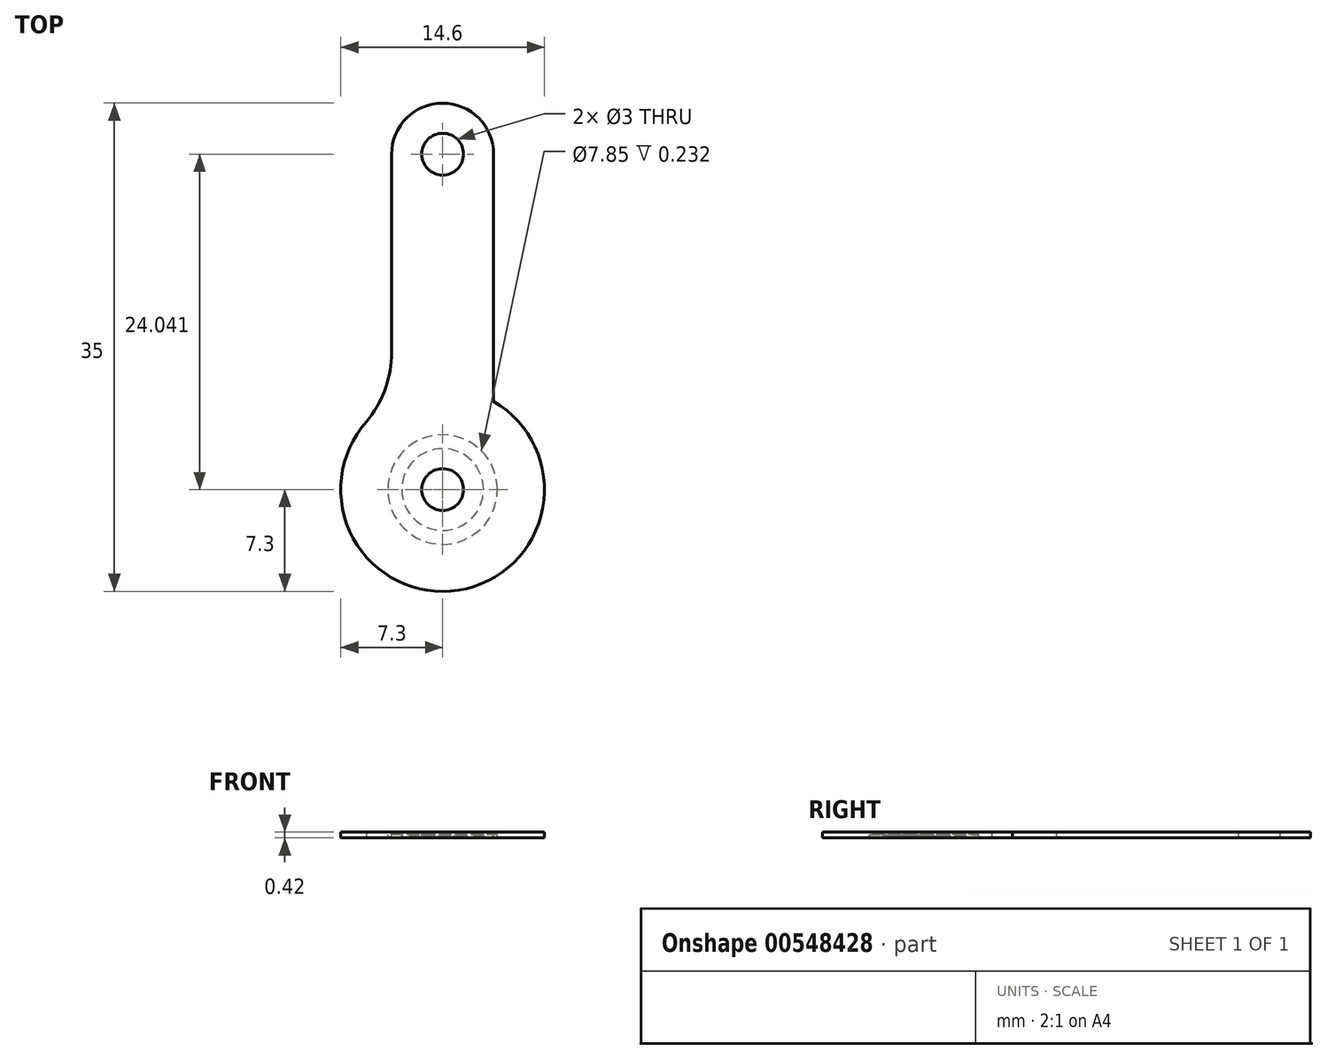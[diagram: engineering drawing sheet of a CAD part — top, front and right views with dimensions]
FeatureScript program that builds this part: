
annotation { "Feature Type Name" : "Feature", "Feature Type Description" : "" }
export const myFeature = defineFeature(function(context is Context, id is Id, definition is map)
    precondition{}
    {
        {
            assignVariable(context, id + "F0", {"name" : "HornCounterBoreDepth", "anyValue" : .42});
        }
        {
            assignVariable(context, id + "F1", {"name" : "HornThick", "anyValue" : 0.23});
        }
        {
            assignVariable(context, id + "F2", {"name" : "HornAxleHoleDepth", "anyValue" : 0.12});
        }
        {
            var Q0;
            Q0=qCreatedBy(makeId("Top.planeOp"),FACE);
            var sketch = newSketch(context, id + "F3", { "sketchPlane" : qUnion([Q0])});
            skCircle(sketch, "E0", {"center": v(0, 0) * mm, "radius": 7.3 * mm});
            skCircle(sketch, "E1", {"center": v(0, 24.04) * mm, "radius": 3.66 * mm});
            skCircle(sketch, "E2", {"center": v(0, 24.04) * mm, "radius": 1.5 * mm});
            skCircle(sketch, "E3", {"center": v(0, 0) * mm, "radius": 1.5 * mm});
            skLineSegment(sketch, "E4", {"start": v(-3.66, 24.04) * mm, "end": v(-3.66, 6.32) * mm});
            skLineSegment(sketch, "E5", {"start": v(3.66, 24.04) * mm, "end": v(3.66, 6.32) * mm});
            skArc(sketch, "E6", {"start": v(-5.43, 4.88) * mm, "mid": v(-4.18, 7.05) * mm, "end": v(-3.66, 9.5) * mm});
            skArc(sketch, "E7.MirrorCS", {"start": v(5.43, 4.88) * mm, "mid": v(4.18, 7.05) * mm, "end": v(3.66, 9.5) * mm});
            skCircle(sketch, "E8", {"center": v(0, 0) * mm, "radius": 2.93 * mm});
            skCircle(sketch, "E9", {"center": v(0, 0) * mm, "radius": 3.92 * mm});
            skSolve(sketch);
        }
        {
            var Q0;
            Q0=makeQuery(id+"F3.imprint","IMPRINT",FACE,{"disambiguationData":[TD([[makeQuery(id+"F3.imprint","IMPRINT",EDGE,{"derivedFrom":sQuery(id+"F3.wireOp",EDGE,"E2")}),-1.0]])]});
            var Q1;
            {var subQ0=sQuery(id+"F3.wireOp",EDGE,"E4");var subQ1=sQuery(id+"F3.wireOp",EDGE,"E0");var subQ2=makeQuery(id+"F3.imprint","INTERSECT",VERTEX,{"derivedFrom":[subQ1,subQ0]});Q1=makeQuery(id+"F3.imprint","IMPRINT",FACE,{"disambiguationData":[TD([[makeQuery(id+"F3.imprint","IMPRINT",EDGE,{"disambiguationData":[TD([[subQ2,1.0]])],"derivedFrom":subQ1}),-1.0]])]});}
            var Q2;
            {var subQ3=sQuery(id+"F3.wireOp",EDGE,"E6");Q2=makeQuery(id+"F3.imprint","IMPRINT",FACE,{"disambiguationData":[TD([[makeQuery(id+"F3.imprint","IMPRINT",EDGE,{"derivedFrom":subQ3}),-1.0]])]});}
            var Q3;
            {var subQ3=sQuery(id+"F3.wireOp",EDGE,"E7.MirrorCS");Q3=makeQuery(id+"F3.imprint","IMPRINT",FACE,{"disambiguationData":[TD([[makeQuery(id+"F3.imprint","IMPRINT",EDGE,{"derivedFrom":subQ3}),1.0]])]});}
            var Q4;
            Q4=makeQuery(id+"F3.imprint","IMPRINT",FACE,{"disambiguationData":[TD([[makeQuery(id+"F3.imprint","IMPRINT",EDGE,{"derivedFrom":sQuery(id+"F3.wireOp",EDGE,"E9")}),-1.0]])]});
            var Q5;
            Q5=makeQuery(id+"F3.imprint","IMPRINT",FACE,{"disambiguationData":[TD([[makeQuery(id+"F3.imprint","IMPRINT",EDGE,{"derivedFrom":sQuery(id+"F3.wireOp",EDGE,"E8")}),-1.0]])]});
            extrude(context, id + "F4", {"entities" : qUnion([Q0, Q1, Q2, Q3, Q4, Q5]), "depth" : (getVariable(context, 'HornThick') - getVariable(context, 'HornCounterBoreDepth')) * mm, "offsetDistance" : 25.4 * mm});
        }
        {
            var Q0;
            Q0=makeQuery(id+"F3.imprint","IMPRINT",FACE,{"disambiguationData":[TD([[makeQuery(id+"F3.imprint","IMPRINT",EDGE,{"derivedFrom":sQuery(id+"F3.wireOp",EDGE,"E2")}),-1.0]])]});
            var Q1;
            {var subQ3=sQuery(id+"F3.wireOp",EDGE,"E7.MirrorCS");Q1=makeQuery(id+"F3.imprint","IMPRINT",FACE,{"disambiguationData":[TD([[makeQuery(id+"F3.imprint","IMPRINT",EDGE,{"derivedFrom":subQ3}),1.0]])]});}
            var Q2;
            {var subQ0=sQuery(id+"F3.wireOp",EDGE,"E4");var subQ1=sQuery(id+"F3.wireOp",EDGE,"E0");var subQ2=makeQuery(id+"F3.imprint","INTERSECT",VERTEX,{"derivedFrom":[subQ1,subQ0]});Q2=makeQuery(id+"F3.imprint","IMPRINT",FACE,{"disambiguationData":[TD([[makeQuery(id+"F3.imprint","IMPRINT",EDGE,{"disambiguationData":[TD([[subQ2,1.0]])],"derivedFrom":subQ1}),-1.0]])]});}
            var Q3;
            {var subQ3=sQuery(id+"F3.wireOp",EDGE,"E6");Q3=makeQuery(id+"F3.imprint","IMPRINT",FACE,{"disambiguationData":[TD([[makeQuery(id+"F3.imprint","IMPRINT",EDGE,{"derivedFrom":subQ3}),-1.0]])]});}
            var Q4;
            Q4=makeQuery(id+"F3.imprint","IMPRINT",FACE,{"disambiguationData":[TD([[makeQuery(id+"F3.imprint","IMPRINT",EDGE,{"derivedFrom":sQuery(id+"F3.wireOp",EDGE,"E9")}),-1.0]])]});
            extrude(context, id + "F5", {"entities" : qUnion([Q0, Q1, Q2, Q3, Q4]), "operationType" : NewBodyOperationType.ADD, "oppositeDirection" : true, "depth" : (getVariable(context, 'HornCounterBoreDepth')) * mm, "offsetDistance" : 25.4 * mm});
        }
        {
            var Q0;
            Q0=makeQuery(id+"F3.imprint","IMPRINT",FACE,{"disambiguationData":[TD([[makeQuery(id+"F3.imprint","IMPRINT",EDGE,{"derivedFrom":sQuery(id+"F3.wireOp",EDGE,"E3")}),-1.0]])]});
            extrude(context, id + "F6", {"entities" : qUnion([Q0]), "operationType" : NewBodyOperationType.ADD, "depth" : (getVariable(context, 'HornThick') - getVariable(context, 'HornCounterBoreDepth') - getVariable(context, 'HornAxleHoleDepth')) * mm, "offsetDistance" : 25.4 * mm});
        }
    });
